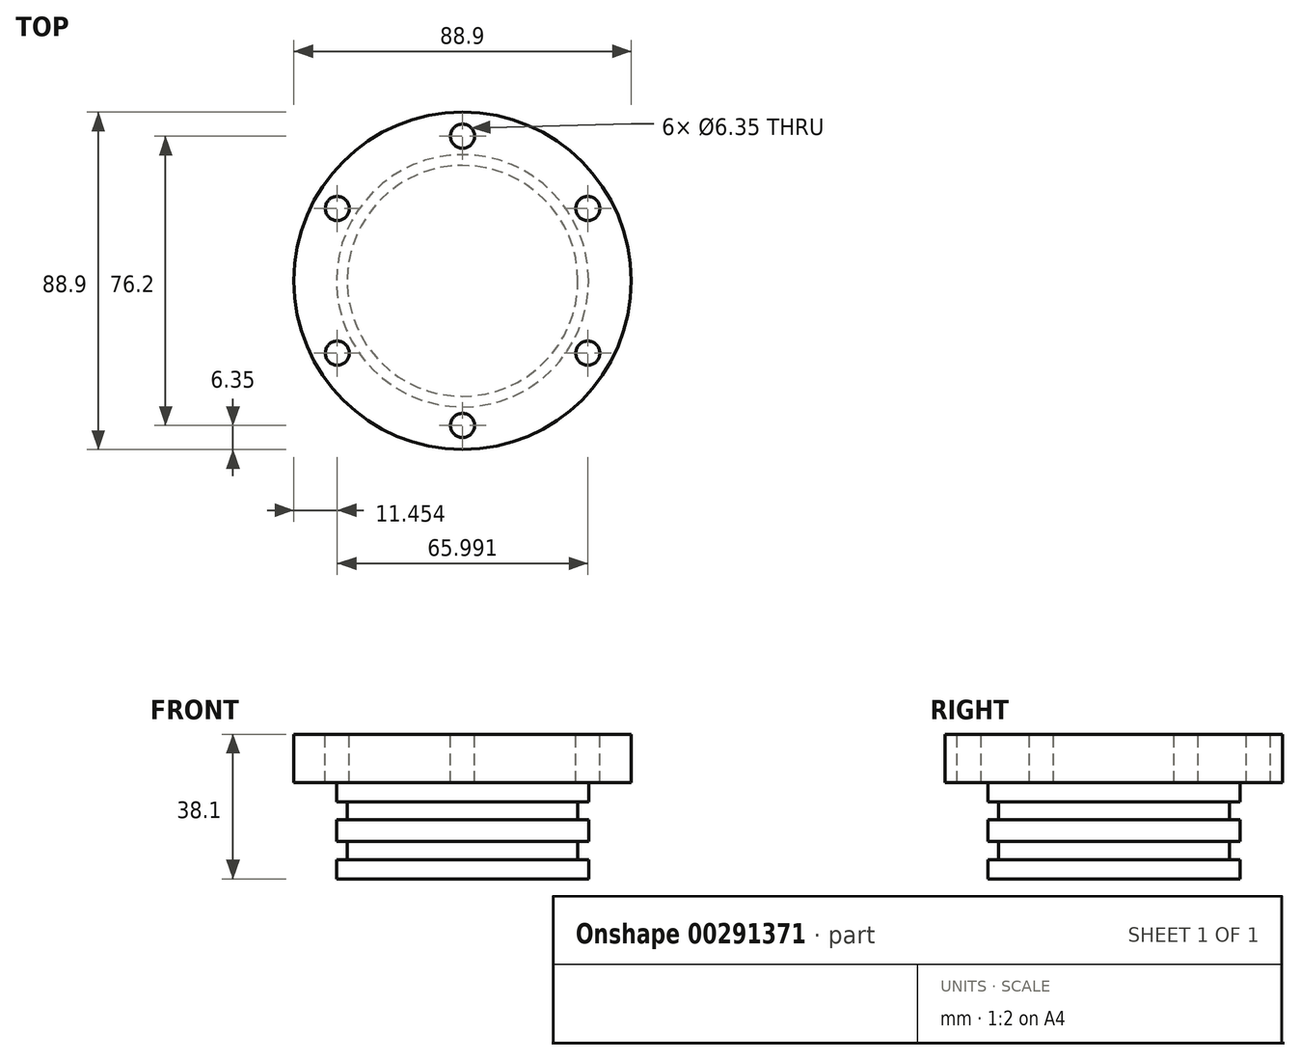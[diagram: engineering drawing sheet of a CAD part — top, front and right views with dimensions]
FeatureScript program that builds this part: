
annotation { "Feature Type Name" : "Feature", "Feature Type Description" : "" }
export const myFeature = defineFeature(function(context is Context, id is Id, definition is map)
    precondition{}
    {
        {
            var Q0;
            Q0=qCreatedBy(makeId("Front.planeOp"),FACE);
            var sketch = newSketch(context, id + "F0", { "sketchPlane" : qUnion([Q0])});
            skLineSegment(sketch, "E0", {"start": v(0, 38.1) * mm, "end": v(44.45, 38.1) * mm});
            skLineSegment(sketch, "E1", {"start": v(44.45, 38.1) * mm, "end": v(44.45, 25.4) * mm});
            skLineSegment(sketch, "E2", {"start": v(44.45, 25.4) * mm, "end": v(33.21, 25.4) * mm});
            skLineSegment(sketch, "E3", {"start": v(33.21, 25.4) * mm, "end": v(33.21, 20.32) * mm});
            skLineSegment(sketch, "E4", {"start": v(33.21, 20.32) * mm, "end": v(30.4, 20.32) * mm});
            skLineSegment(sketch, "E5", {"start": v(30.4, 20.32) * mm, "end": v(30.4, 15.57) * mm});
            skLineSegment(sketch, "E6", {"start": v(30.4, 15.57) * mm, "end": v(33.21, 15.57) * mm});
            skLineSegment(sketch, "E7", {"start": v(33.21, 15.57) * mm, "end": v(33.21, 9.83) * mm});
            skLineSegment(sketch, "E8", {"start": v(33.21, 9.83) * mm, "end": v(30.4, 9.83) * mm});
            skLineSegment(sketch, "E9", {"start": v(30.4, 9.83) * mm, "end": v(30.4, 5.08) * mm});
            skLineSegment(sketch, "E10", {"start": v(30.4, 5.08) * mm, "end": v(33.21, 5.08) * mm});
            skLineSegment(sketch, "E11", {"start": v(33.21, 5.08) * mm, "end": v(33.21, 0) * mm});
            skLineSegment(sketch, "E12", {"start": v(33.21, 0) * mm, "end": v(0, 0) * mm});
            skLineSegment(sketch, "E13", {"start": v(0, 38.1) * mm, "end": v(0, 0) * mm});
            skSolve(sketch);
        }
        {
            var Q0;
            Q0=makeQuery(id+"F0.imprint","IMPRINT",FACE,{"disambiguationData":[TD([[makeQuery(id+"F0.imprint","IMPRINT",EDGE,{"derivedFrom":sQuery(id+"F0.wireOp",EDGE,"E0")}),-1.0]])]});
            var sketch = newSketch(context, id + "F1", { "sketchPlane" : qUnion([Q0])});
            skLineSegment(sketch, "E14", {"start": v(0, 87.9) * mm, "end": v(0, -14.54) * mm, "construction": true});
            skSolve(sketch);
        }
        {
            var Q0;
            Q0=makeQuery(id+"F0.imprint","IMPRINT",FACE,{"disambiguationData":[TD([[makeQuery(id+"F0.imprint","IMPRINT",EDGE,{"derivedFrom":sQuery(id+"F0.wireOp",EDGE,"E0")}),-1.0]])]});
            var Q1;
            Q1=sQuery(id+"F1.wireOp",EDGE,"E14");
            revolve(context, id + "F2", {"entities" : qUnion([Q0]), "axis" : qUnion([Q1]), "revolveType" : RevolveType.FULL});
        }
        {
            var Q0;
            Q0=makeQuery(id+"F2.opRevolve","SWEPT_FACE",FACE,{"disambiguationData":[OSD([sQuery(id+"F0.wireOp",EDGE,"E0")])]});
            var sketch = newSketch(context, id + "F3", { "sketchPlane" : qUnion([Q0])});
            skCircle(sketch, "E15", {"center": v(0, 38.1) * mm, "radius": 3.17 * mm});
            skCircle(sketch, "E16.1.0", {"center": v(33, 19.05) * mm, "radius": 3.17 * mm});
            skCircle(sketch, "E16.2.0", {"center": v(33, -19.05) * mm, "radius": 3.17 * mm});
            skCircle(sketch, "E16.3.0", {"center": v(0, -38.1) * mm, "radius": 3.17 * mm});
            skCircle(sketch, "E16.4.0", {"center": v(-33, -19.05) * mm, "radius": 3.17 * mm});
            skCircle(sketch, "E16.5.0", {"center": v(-33, 19.05) * mm, "radius": 3.17 * mm});
            skPoint(sketch, "E16.center", {"position": v(0, 0) * mm});
            skLineSegment(sketch, "E16.anchor1", {"start": v(0, 0) * mm, "end": v(0, 38.1) * mm, "construction": true});
            skLineSegment(sketch, "E16.anchor2", {"start": v(0, 0) * mm, "end": v(-33, 19.05) * mm, "construction": true});
            skSolve(sketch);
        }
        {
            var Q0;
            Q0=makeQuery(id+"F3.imprint","IMPRINT",FACE,{"disambiguationData":[TD([[makeQuery(id+"F3.imprint","IMPRINT",EDGE,{"derivedFrom":sQuery(id+"F3.wireOp",EDGE,"E16.3.0")}),1.0]])]});
            var Q1;
            Q1=makeQuery(id+"F3.imprint","IMPRINT",FACE,{"disambiguationData":[TD([[makeQuery(id+"F3.imprint","IMPRINT",EDGE,{"derivedFrom":sQuery(id+"F3.wireOp",EDGE,"E16.2.0")}),1.0]])]});
            var Q2;
            Q2=makeQuery(id+"F3.imprint","IMPRINT",FACE,{"disambiguationData":[TD([[makeQuery(id+"F3.imprint","IMPRINT",EDGE,{"derivedFrom":sQuery(id+"F3.wireOp",EDGE,"E16.1.0")}),1.0]])]});
            var Q3;
            Q3=makeQuery(id+"F3.imprint","IMPRINT",FACE,{"disambiguationData":[TD([[makeQuery(id+"F3.imprint","IMPRINT",EDGE,{"derivedFrom":sQuery(id+"F3.wireOp",EDGE,"E15")}),1.0]])]});
            var Q4;
            Q4=makeQuery(id+"F3.imprint","IMPRINT",FACE,{"disambiguationData":[TD([[makeQuery(id+"F3.imprint","IMPRINT",EDGE,{"derivedFrom":sQuery(id+"F3.wireOp",EDGE,"E16.5.0")}),1.0]])]});
            var Q5;
            Q5=makeQuery(id+"F3.imprint","IMPRINT",FACE,{"disambiguationData":[TD([[makeQuery(id+"F3.imprint","IMPRINT",EDGE,{"derivedFrom":sQuery(id+"F3.wireOp",EDGE,"E16.4.0")}),1.0]])]});
            extrude(context, id + "F4", {"entities" : qUnion([Q0, Q1, Q2, Q3, Q4, Q5]), "operationType" : NewBodyOperationType.REMOVE, "oppositeDirection" : true, "depth" : 25.4 * mm});
        }
    });
